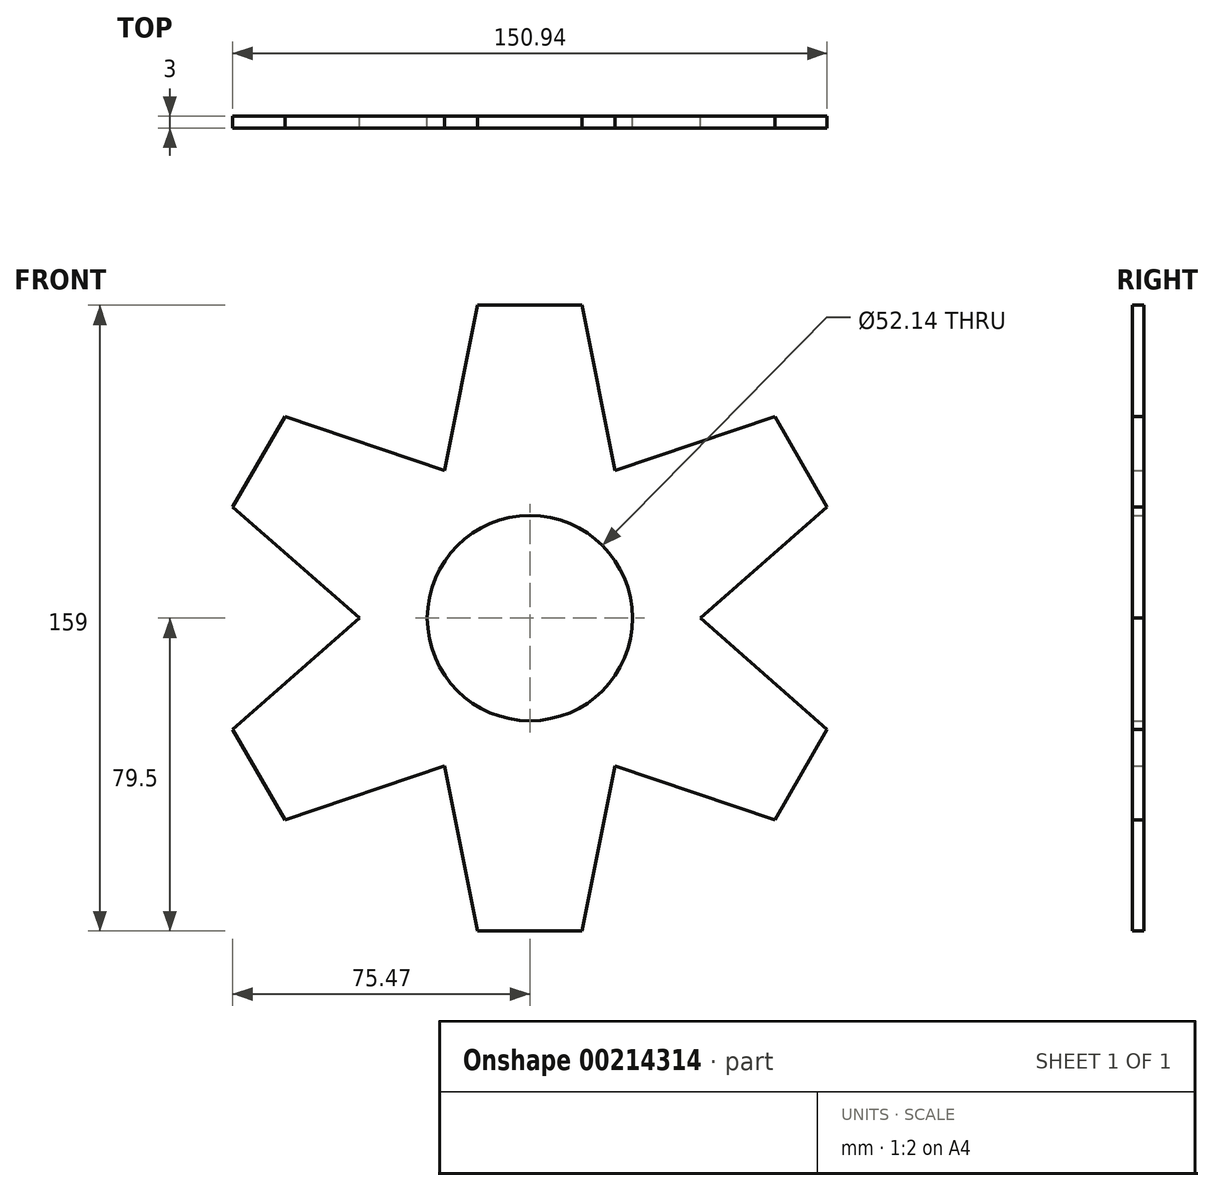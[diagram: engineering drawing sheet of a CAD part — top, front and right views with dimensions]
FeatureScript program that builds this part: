
annotation { "Feature Type Name" : "Feature", "Feature Type Description" : "" }
export const myFeature = defineFeature(function(context is Context, id is Id, definition is map)
    precondition{}
    {
        {
            var Q0;
            Q0=qCreatedBy(makeId("Front.planeOp"),FACE);
            var sketch = newSketch(context, id + "F0", { "sketchPlane" : qUnion([Q0])});
            skCircle(sketch, "E0", {"center": v(0, 0) * mm, "radius": 37.5 * mm, "construction": true});
            skLineSegment(sketch, "E1.0", {"start": v(-21.65, 37.5) * mm, "end": v(21.65, 37.5) * mm});
            skLineSegment(sketch, "E1.1", {"start": v(21.65, 37.5) * mm, "end": v(43.3, 0) * mm});
            skLineSegment(sketch, "E1.2", {"start": v(43.3, 0) * mm, "end": v(21.65, -37.5) * mm});
            skLineSegment(sketch, "E1.3", {"start": v(21.65, -37.5) * mm, "end": v(-21.65, -37.5) * mm});
            skLineSegment(sketch, "E1.4", {"start": v(-21.65, -37.5) * mm, "end": v(-43.3, 0) * mm});
            skLineSegment(sketch, "E1.5", {"start": v(-43.3, 0) * mm, "end": v(-21.65, 37.5) * mm});
            skPoint(sketch, "E1.0.midPoint", {"position": v(0, 37.5) * mm});
            skLineSegment(sketch, "E2", {"start": v(0, 37.5) * mm, "end": v(0, 79.5) * mm});
            skLineSegment(sketch, "E3.bottom", {"start": v(13.25, 79.5) * mm, "end": v(-13.25, 79.5) * mm});
            skLineSegment(sketch, "E3.top", {"start": v(13.25, 79.5) * mm, "end": v(-13.25, 79.5) * mm});
            skLineSegment(sketch, "E3.left", {"start": v(13.25, 79.5) * mm, "end": v(13.25, 79.5) * mm});
            skLineSegment(sketch, "E3.right", {"start": v(-13.25, 79.5) * mm, "end": v(-13.25, 79.5) * mm});
            skPoint(sketch, "E3.middle", {"position": v(0, 79.5) * mm});
            skLineSegment(sketch, "E4", {"start": v(13.25, 79.5) * mm, "end": v(21.65, 37.5) * mm});
            skLineSegment(sketch, "E5", {"start": v(-13.25, 79.5) * mm, "end": v(-21.65, 37.5) * mm});
            skLineSegment(sketch, "E6", {"start": v(0, -37.5) * mm, "end": v(0, -79.5) * mm});
            skLineSegment(sketch, "E7.bottom", {"start": v(13.25, -79.5) * mm, "end": v(-13.25, -79.5) * mm});
            skLineSegment(sketch, "E7.top", {"start": v(13.25, -79.5) * mm, "end": v(-13.25, -79.5) * mm});
            skLineSegment(sketch, "E7.left", {"start": v(13.25, -79.5) * mm, "end": v(13.25, -79.5) * mm});
            skLineSegment(sketch, "E7.right", {"start": v(-13.25, -79.5) * mm, "end": v(-13.25, -79.5) * mm});
            skPoint(sketch, "E7.middle", {"position": v(0, -79.5) * mm});
            skLineSegment(sketch, "E8", {"start": v(13.25, -79.5) * mm, "end": v(21.65, -37.5) * mm});
            skLineSegment(sketch, "E9", {"start": v(-13.25, -79.5) * mm, "end": v(-21.65, -37.5) * mm});
            skLineSegment(sketch, "E10", {"start": v(-32.48, -18.75) * mm, "end": v(-68.85, -39.75) * mm});
            skPoint(sketch, "E11.middle", {"position": v(-68.85, -39.75) * mm});
            skLineSegment(sketch, "E12", {"start": v(-68.85, -39.75) * mm, "end": v(-62.22, -51.22) * mm});
            skLineSegment(sketch, "E13", {"start": v(-68.85, -39.75) * mm, "end": v(-75.47, -28.28) * mm});
            skLineSegment(sketch, "E14", {"start": v(-62.22, -51.22) * mm, "end": v(-21.65, -37.5) * mm});
            skLineSegment(sketch, "E15", {"start": v(-75.47, -28.28) * mm, "end": v(-43.3, 0) * mm});
            skLineSegment(sketch, "E16", {"start": v(-43.3, 0) * mm, "end": v(-75.47, 28.28) * mm});
            skLineSegment(sketch, "E17", {"start": v(-75.47, 28.28) * mm, "end": v(-62.22, 51.22) * mm});
            skLineSegment(sketch, "E18", {"start": v(-62.22, 51.22) * mm, "end": v(-21.65, 37.5) * mm});
            skLineSegment(sketch, "E19", {"start": v(21.65, 37.5) * mm, "end": v(62.22, 51.22) * mm});
            skLineSegment(sketch, "E20", {"start": v(62.22, 51.22) * mm, "end": v(75.47, 28.28) * mm});
            skLineSegment(sketch, "E21", {"start": v(75.47, 28.28) * mm, "end": v(43.3, 0) * mm});
            skLineSegment(sketch, "E22", {"start": v(43.3, 0) * mm, "end": v(75.47, -28.28) * mm});
            skLineSegment(sketch, "E23", {"start": v(75.47, -28.28) * mm, "end": v(62.22, -51.22) * mm});
            skLineSegment(sketch, "E24", {"start": v(62.22, -51.22) * mm, "end": v(21.65, -37.5) * mm});
            skCircle(sketch, "E25", {"center": v(0, 0) * mm, "radius": 26.07 * mm});
            skCircle(sketch, "E26", {"center": v(0, 0) * mm, "radius": 80.6 * mm, "construction": true});
            skSolve(sketch);
        }
        {
            var Q0;
            Q0 = qSketchRegion(id + "F0", true);
            extrude(context, id + "F1", {"entities" : qUnion([Q0]), "depth" : 3 * mm, "offsetDistance" : 25 * mm});
        }
    });
